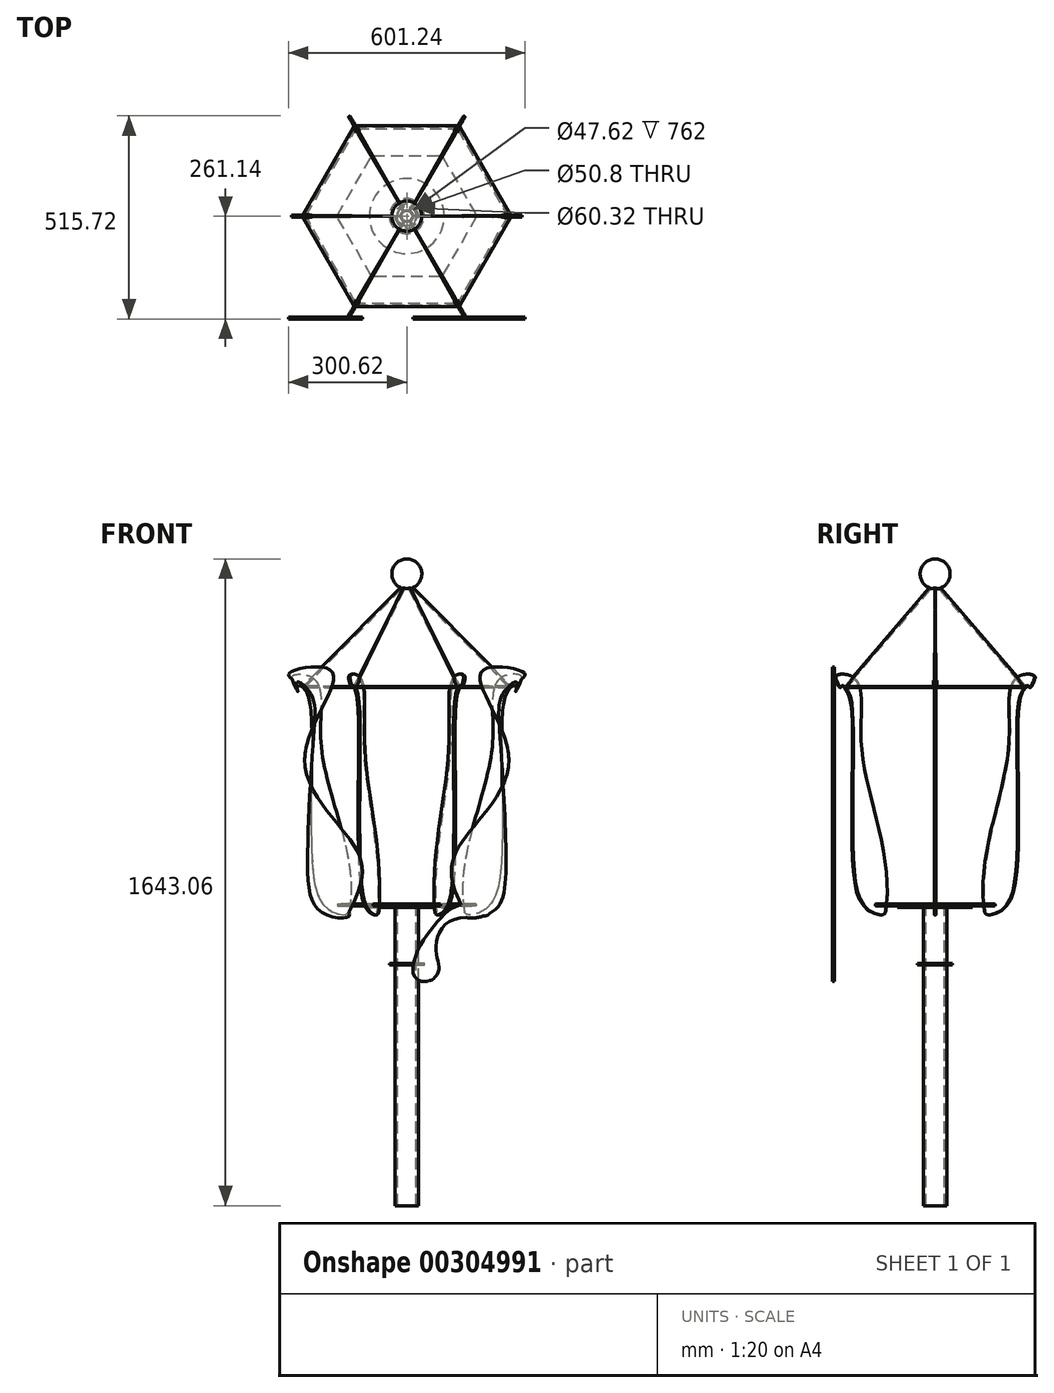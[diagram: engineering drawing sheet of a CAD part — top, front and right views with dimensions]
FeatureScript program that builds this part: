
annotation { "Feature Type Name" : "Feature", "Feature Type Description" : "" }
export const myFeature = defineFeature(function(context is Context, id is Id, definition is map)
    precondition{}
    {
        {
            var Q0;
            Q0=qCreatedBy(makeId("Front.planeOp"),FACE);
            var sketch = newSketch(context, id + "F0", { "sketchPlane" : qUnion([Q0])});
            skFitSpline(sketch, "E0", {"points": [v(-291.6, 220.03) * mm, v(-241.23, 224.84) * mm, v(-217, 46.23) * mm, v(-146.46, -370.89) * mm], "startDerivative": vector(-130.21, 261.55) * mm, "endDerivative": vector(-153.32, -857.59) * mm});
            skPoint(sketch, "E1.1.internal.snap0", {"position": v(-274.64, 203.2) * mm});
            skFitSpline(sketch, "E1", {"points": [v(-291.6, 220.03) * mm, v(-274.64, 203.2) * mm, v(-257.97, 191.77) * mm, v(-241.35, 95.06) * mm, v(-239.01, -260.8) * mm, v(-195.03, -367.33) * mm, v(-146.46, -370.89) * mm], "startDerivative": vector(512.54, -1083.48) * mm, "endDerivative": vector(69.83, 321.72) * mm});
            skPoint(sketch, "E2", {"position": v(-173.04, -355.6) * mm});
            skLineSegment(sketch, "E3", {"start": v(0, 533.4) * mm, "end": v(0, -533.4) * mm, "construction": true});
            skArc(sketch, "E4", {"start": v(0, 525.46) * mm, "mid": v(-38.1, 487.36) * mm, "end": v(0, 449.26) * mm});
            skLineSegment(sketch, "E5", {"start": v(0, 525.46) * mm, "end": v(0, 449.26) * mm});
            skPoint(sketch, "E6", {"position": v(0, 461.96) * mm});
            skLineSegment(sketch, "E7.bottom", {"start": v(-30.16, -355.6) * mm, "end": v(-23.81, -355.6) * mm});
            skLineSegment(sketch, "E7.top", {"start": v(-30.16, -1117.6) * mm, "end": v(-23.81, -1117.6) * mm});
            skLineSegment(sketch, "E7.left", {"start": v(-30.16, -355.6) * mm, "end": v(-30.16, -1117.6) * mm});
            skLineSegment(sketch, "E7.right", {"start": v(-23.81, -355.6) * mm, "end": v(-23.81, -1117.6) * mm});
            skFitSpline(sketch, "E8.MirrorCS", {"points": [v(291.6, 220.03) * mm, v(274.64, 203.2) * mm, v(257.97, 191.77) * mm, v(241.35, 95.06) * mm, v(239.01, -260.8) * mm, v(195.03, -367.33) * mm, v(146.46, -370.89) * mm], "startDerivative": vector(-512.54, -1083.48) * mm, "endDerivative": vector(-69.83, 321.72) * mm});
            skPoint(sketch, "E9.MirrorP", {"position": v(173.04, -355.6) * mm});
            skFitSpline(sketch, "E10.MirrorCS", {"points": [v(291.6, 220.03) * mm, v(241.23, 224.84) * mm, v(217, 46.23) * mm, v(146.46, -370.89) * mm], "startDerivative": vector(130.21, 261.55) * mm, "endDerivative": vector(153.32, -857.59) * mm});
            skLineSegment(sketch, "E11.MirrorCS", {"start": v(30.16, -355.6) * mm, "end": v(30.16, -1117.6) * mm});
            skLineSegment(sketch, "E12.MirrorCS", {"start": v(30.16, -355.6) * mm, "end": v(23.81, -355.6) * mm});
            skLineSegment(sketch, "E13.MirrorCS", {"start": v(23.81, -355.6) * mm, "end": v(23.81, -1117.6) * mm});
            skLineSegment(sketch, "E14.MirrorCS", {"start": v(30.16, -1117.6) * mm, "end": v(23.81, -1117.6) * mm});
            skFitSpline(sketch, "E15", {"points": [v(183.47, -350.73) * mm, v(204.81, -367.22) * mm, v(125.26, -406.15) * mm, v(80.03, -477) * mm, v(76.64, -518.47) * mm, v(56.5, -545.64) * mm, v(30.16, -533.12) * mm, v(33.54, -472.55) * mm, v(77.47, -401.03) * mm, v(128.65, -357.22) * mm, v(183.47, -350.73) * mm]});
            skSolve(sketch);
        }
        {
            var Q0;
            Q0=qCreatedBy(makeId("Top.planeOp"),FACE);
            cPlane(context, id + "F1", {"entities" : qUnion([Q0]), "cplaneType" : CPlaneType.OFFSET, "offset" : 355.6 * mm, "oppositeDirection" : true, "width" : 152.4 * mm, "height" : 152.4 * mm});
        }
        {
            var Q0;
            Q0=qCreatedBy(id+"F1.planeOp",FACE);
            var sketch = newSketch(context, id + "F2", { "sketchPlane" : qUnion([Q0])});
            skCircle(sketch, "E16.cCircle", {"center": v(0, 0) * mm, "radius": 177.8 * mm, "construction": true});
            skLineSegment(sketch, "E16.0", {"start": v(-177.8, 0) * mm, "end": v(-88.9, 153.98) * mm});
            skLineSegment(sketch, "E16.1", {"start": v(-88.9, 153.98) * mm, "end": v(88.9, 153.98) * mm});
            skLineSegment(sketch, "E16.2", {"start": v(88.9, 153.98) * mm, "end": v(177.8, 0) * mm});
            skLineSegment(sketch, "E16.3", {"start": v(177.8, 0) * mm, "end": v(88.9, -153.98) * mm});
            skLineSegment(sketch, "E16.4", {"start": v(88.9, -153.98) * mm, "end": v(-88.9, -153.98) * mm});
            skLineSegment(sketch, "E16.5", {"start": v(-88.9, -153.98) * mm, "end": v(-177.8, 0) * mm});
            skLineSegment(sketch, "E17", {"start": v(-176.43, 2.38) * mm, "end": v(-149.22, 2.38) * mm});
            skLineSegment(sketch, "E18", {"start": v(-149.22, 2.38) * mm, "end": v(-149.22, -2.38) * mm});
            skLineSegment(sketch, "E19", {"start": v(-149.22, -2.38) * mm, "end": v(-176.43, -2.38) * mm});
            skPoint(sketch, "E20.endSnap0", {"position": v(-149.22, 0) * mm});
            skLineSegment(sketch, "E21", {"start": v(0, 0) * mm, "end": v(-304.8, 0) * mm, "construction": true});
            skPoint(sketch, "E22.1.0", {"position": v(-74.61, -129.23) * mm});
            skLineSegment(sketch, "E22.1.1", {"start": v(-72.55, -130.42) * mm, "end": v(-86.15, -153.98) * mm});
            skLineSegment(sketch, "E22.1.2", {"start": v(-76.67, -128.04) * mm, "end": v(-72.55, -130.42) * mm});
            skLineSegment(sketch, "E22.1.3", {"start": v(-90.27, -151.6) * mm, "end": v(-76.67, -128.04) * mm});
            skPoint(sketch, "E22.2.0", {"position": v(74.61, -129.23) * mm});
            skLineSegment(sketch, "E22.2.1", {"start": v(76.67, -128.04) * mm, "end": v(90.27, -151.6) * mm});
            skLineSegment(sketch, "E22.2.2", {"start": v(72.55, -130.42) * mm, "end": v(76.67, -128.04) * mm});
            skLineSegment(sketch, "E22.2.3", {"start": v(86.15, -153.98) * mm, "end": v(72.55, -130.42) * mm});
            skPoint(sketch, "E23.0.3.0", {"position": v(149.22, 0) * mm});
            skLineSegment(sketch, "E23.1.3.0", {"start": v(149.22, 2.38) * mm, "end": v(176.43, 2.38) * mm});
            skLineSegment(sketch, "E23.4.3.0", {"start": v(149.22, -2.38) * mm, "end": v(149.22, 2.38) * mm});
            skLineSegment(sketch, "E23.7.3.0", {"start": v(176.43, -2.38) * mm, "end": v(149.22, -2.38) * mm});
            skPoint(sketch, "E23.0.4.0", {"position": v(74.61, 129.23) * mm});
            skLineSegment(sketch, "E23.1.4.0", {"start": v(72.55, 130.42) * mm, "end": v(86.15, 153.98) * mm});
            skLineSegment(sketch, "E23.4.4.0", {"start": v(76.67, 128.04) * mm, "end": v(72.55, 130.42) * mm});
            skLineSegment(sketch, "E23.7.4.0", {"start": v(90.27, 151.6) * mm, "end": v(76.67, 128.04) * mm});
            skPoint(sketch, "E23.0.5.0", {"position": v(-74.61, 129.23) * mm});
            skLineSegment(sketch, "E23.1.5.0", {"start": v(-76.67, 128.04) * mm, "end": v(-90.27, 151.6) * mm});
            skLineSegment(sketch, "E23.4.5.0", {"start": v(-72.55, 130.42) * mm, "end": v(-76.67, 128.04) * mm});
            skLineSegment(sketch, "E23.7.5.0", {"start": v(-86.15, 153.98) * mm, "end": v(-72.55, 130.42) * mm});
            skSolve(sketch);
        }
        {
            var Q0;
            {var subQ11=sQuery(id+"F2.wireOp",EDGE,"E17");Q0=makeQuery(id+"F2.imprint","IMPRINT",FACE,{"disambiguationData":[TD([[makeQuery(id+"F2.imprint","IMPRINT",EDGE,{"derivedFrom":subQ11}),1.0]])]});}
            extrude(context, id + "F3", {"entities" : qUnion([Q0]), "depth" : 4.76 * mm});
        }
        {
            var Q0;
            Q0=qCreatedBy(makeId("Top.planeOp"),FACE);
            cPlane(context, id + "F4", {"entities" : qUnion([Q0]), "cplaneType" : CPlaneType.OFFSET, "offset" : 203.2 * mm, "width" : 152.4 * mm, "height" : 152.4 * mm});
        }
        {
            var Q0;
            Q0=qCreatedBy(id+"F4.planeOp",FACE);
            var sketch = newSketch(context, id + "F5", { "sketchPlane" : qUnion([Q0])});
            skCircle(sketch, "E24.cCircle", {"center": v(0, 0) * mm, "radius": 222.25 * mm, "construction": true});
            skLineSegment(sketch, "E24.0", {"start": v(-128.32, -222.25) * mm, "end": v(-256.63, 0) * mm});
            skLineSegment(sketch, "E24.1", {"start": v(-256.63, 0) * mm, "end": v(-128.32, 222.25) * mm});
            skLineSegment(sketch, "E24.2", {"start": v(-128.32, 222.25) * mm, "end": v(128.32, 222.25) * mm});
            skLineSegment(sketch, "E24.3", {"start": v(128.32, 222.25) * mm, "end": v(256.63, 0) * mm});
            skLineSegment(sketch, "E24.4", {"start": v(256.63, 0) * mm, "end": v(128.32, -222.25) * mm});
            skLineSegment(sketch, "E24.5", {"start": v(128.32, -222.25) * mm, "end": v(-128.32, -222.25) * mm});
            skPoint(sketch, "E24.0.midPoint", {"position": v(-192.47, -111.12) * mm});
            skLineSegment(sketch, "E25", {"start": v(-255.26, -2.38) * mm, "end": v(-231.23, -2.38) * mm});
            skLineSegment(sketch, "E26", {"start": v(-231.23, -2.38) * mm, "end": v(-231.23, 2.38) * mm});
            skLineSegment(sketch, "E27", {"start": v(-231.23, 2.38) * mm, "end": v(-255.26, 2.38) * mm});
            skLineSegment(sketch, "E28", {"start": v(0, 0) * mm, "end": v(-304.8, 0) * mm, "construction": true});
            skPoint(sketch, "E29", {"position": v(-231.23, 0) * mm});
            skPoint(sketch, "E30.1.0", {"position": v(-115.62, -200.25) * mm});
            skLineSegment(sketch, "E30.1.1", {"start": v(-125.57, -222.25) * mm, "end": v(-113.55, -201.44) * mm});
            skLineSegment(sketch, "E30.1.2", {"start": v(-117.68, -199.06) * mm, "end": v(-129.7, -219.87) * mm});
            skLineSegment(sketch, "E30.1.3", {"start": v(-113.55, -201.44) * mm, "end": v(-117.68, -199.06) * mm});
            skPoint(sketch, "E30.2.0", {"position": v(115.62, -200.25) * mm});
            skLineSegment(sketch, "E30.2.1", {"start": v(129.7, -219.87) * mm, "end": v(117.68, -199.06) * mm});
            skLineSegment(sketch, "E30.2.2", {"start": v(113.55, -201.44) * mm, "end": v(125.57, -222.25) * mm});
            skLineSegment(sketch, "E30.2.3", {"start": v(117.68, -199.06) * mm, "end": v(113.55, -201.44) * mm});
            skPoint(sketch, "E30.3.0", {"position": v(231.23, 0) * mm});
            skLineSegment(sketch, "E30.3.1", {"start": v(255.26, 2.38) * mm, "end": v(231.23, 2.38) * mm});
            skLineSegment(sketch, "E30.3.2", {"start": v(231.23, -2.38) * mm, "end": v(255.26, -2.38) * mm});
            skLineSegment(sketch, "E30.3.3", {"start": v(231.23, 2.38) * mm, "end": v(231.23, -2.38) * mm});
            skPoint(sketch, "E30.4.0", {"position": v(115.62, 200.25) * mm});
            skLineSegment(sketch, "E30.4.1", {"start": v(125.57, 222.25) * mm, "end": v(113.55, 201.44) * mm});
            skLineSegment(sketch, "E30.4.2", {"start": v(117.68, 199.06) * mm, "end": v(129.7, 219.87) * mm});
            skLineSegment(sketch, "E30.4.3", {"start": v(113.55, 201.44) * mm, "end": v(117.68, 199.06) * mm});
            skPoint(sketch, "E30.5.0", {"position": v(-115.62, 200.25) * mm});
            skLineSegment(sketch, "E30.5.1", {"start": v(-129.7, 219.87) * mm, "end": v(-117.68, 199.06) * mm});
            skLineSegment(sketch, "E30.5.2", {"start": v(-113.55, 201.44) * mm, "end": v(-125.57, 222.25) * mm});
            skLineSegment(sketch, "E30.5.3", {"start": v(-117.68, 199.06) * mm, "end": v(-113.55, 201.44) * mm});
            skSolve(sketch);
        }
        {
            var Q0;
            {var subQ11=sQuery(id+"F5.wireOp",EDGE,"E25");Q0=makeQuery(id+"F5.imprint","IMPRINT",FACE,{"disambiguationData":[TD([[makeQuery(id+"F5.imprint","IMPRINT",EDGE,{"derivedFrom":subQ11}),-1.0]])]});}
            extrude(context, id + "F6", {"entities" : qUnion([Q0]), "oppositeDirection" : true, "depth" : 4.76 * mm});
        }
        {
            var Q0;
            Q0=makeQuery(id+"F0.imprint","IMPRINT",FACE,{"disambiguationData":[TD([[makeQuery(id+"F0.imprint","IMPRINT",EDGE,{"derivedFrom":sQuery(id+"F0.wireOp",EDGE,"E0")}),-1.0]])]});
            var Q1;
            {var subQ1=sQuery(id+"F0.wireOp",EDGE,"E8.MirrorCS");Q1=makeQuery(id+"F0.imprint","IMPRINT",FACE,{"disambiguationData":[TD([[makeQuery(id+"F0.imprint","IMPRINT",EDGE,{"derivedFrom":subQ1}),-1.0]])]});}
            extrude(context, id + "F7", {"entities" : qUnion([Q0, Q1]), "endBound" : BoundingType.SYMMETRIC, "depth" : 4.76 * mm});
        }
        {
            var Q0;
            Q0=makeQuery(id+"F7.opExtrude","SWEPT_BODY",BODY,{"disambiguationData":[OSD([sQuery(id+"F0.wireOp",EDGE,"E0"),sQuery(id+"F0.wireOp",EDGE,"E1")])]});
            var Q1;
            Q1=makeQuery(id+"F7.opExtrude","SWEPT_BODY",BODY,{"disambiguationData":[OSD([sQuery(id+"F0.wireOp",EDGE,"E8.MirrorCS"),sQuery(id+"F0.wireOp",EDGE,"E10.MirrorCS"),sQuery(id+"F0.wireOp",EDGE,"E11.MirrorCS"),sQuery(id+"F0.wireOp",EDGE,"E15")])]});
            var Q2;
            Q2=sQuery(id+"F0.wireOp",EDGE,"E3");
            circularPattern(context, id + "F8", {"entities" : qUnion([Q0, Q1]), "axis" : qUnion([Q2]), "angle" : 360 * degree, "instanceCount" : 3, "equalSpace" : true});
        }
        {
            var Q0;
            Q0=makeQuery(id+"F0.imprint","IMPRINT",FACE,{"disambiguationData":[TD([[makeQuery(id+"F0.imprint","IMPRINT",EDGE,{"derivedFrom":sQuery(id+"F0.wireOp",EDGE,"E4")}),1.0]])]});
            var Q1;
            Q1=makeQuery(id+"F0.imprint","IMPRINT",FACE,{"disambiguationData":[TD([[makeQuery(id+"F0.imprint","IMPRINT",EDGE,{"derivedFrom":sQuery(id+"F0.wireOp",EDGE,"E7.bottom")}),-1.0]])]});
            var Q2;
            Q2=sQuery(id+"F0.wireOp",EDGE,"E3");
            revolve(context, id + "F9", {"entities" : qUnion([Q0, Q1]), "axis" : qUnion([Q2]), "revolveType" : RevolveType.FULL});
        }
        {
            var Q0;
            Q0=makeQuery(id+"F6.opExtrude","CAP_VERTEX",VERTEX,{"disambiguationData":[OSD([sQuery(id+"F5.wireOp",EDGE,"E24.0"),sQuery(id+"F5.wireOp",EDGE,"E25")])],"isStart":true});
            var Q1;
            Q1=makeQuery(id+"F6.opExtrude","CAP_VERTEX",VERTEX,{"disambiguationData":[OSD([sQuery(id+"F5.wireOp",EDGE,"E24.0"),sQuery(id+"F5.wireOp",EDGE,"E30.1.2")])],"isStart":true});
            var Q2;
            Q2=sQuery(id+"F0.wireOp",VERTEX,"E6");
            cPlane(context, id + "F10", {"entities" : qUnion([Q0, Q1, Q2]), "cplaneType" : CPlaneType.THREE_POINT, "offset" : 25.4 * mm, "width" : 152.4 * mm, "height" : 152.4 * mm});
        }
        {
            var Q0;
            Q0=qCreatedBy(id+"F10.planeOp",FACE);
            var sketch = newSketch(context, id + "F11", { "sketchPlane" : qUnion([Q0])});
            skLineSegment(sketch, "E31.0.7", {"start": v(120.81, -35.47) * mm, "end": v(-114.24, 52.95) * mm, "construction": true});
            skPoint(sketch, "E32.0", {"position": v(123.39, 328) * mm});
            skLineSegment(sketch, "E33", {"start": v(123.39, 328) * mm, "end": v(-114.24, 52.95) * mm, "construction": true});
            skLineSegment(sketch, "E34", {"start": v(120.81, -35.47) * mm, "end": v(123.39, 328) * mm, "construction": true});
            skLineSegment(sketch, "E35.0", {"start": v(108.66, 314.6) * mm, "end": v(-105.95, 66.2) * mm});
            skLineSegment(sketch, "E35.1", {"start": v(123.3, -20.05) * mm, "end": v(125.63, 308.21) * mm});
            skLineSegment(sketch, "E35.2", {"start": v(120.81, -42.25) * mm, "end": v(-118.7, 47.85) * mm});
            skPoint(sketch, "E36.0", {"position": v(130.17, 346.04) * mm});
            skArc(sketch, "E37", {"start": v(125.63, 308.21) * mm, "mid": v(116.76, 310.38) * mm, "end": v(108.66, 314.6) * mm});
            skLineSegment(sketch, "E38", {"start": v(123.3, -20.05) * mm, "end": v(120.92, -20.03) * mm});
            skLineSegment(sketch, "E39", {"start": v(120.92, -20.03) * mm, "end": v(120.81, -42.25) * mm});
            skLineSegment(sketch, "E40", {"start": v(130.17, 346.04) * mm, "end": v(3.29, 8.74) * mm, "construction": true});
            skPoint(sketch, "E40.endSnap0", {"position": v(3.29, 8.74) * mm});
            skLineSegment(sketch, "E41.MirrorCS", {"start": v(-105.95, 66.2) * mm, "end": v(-104.14, 64.64) * mm});
            skLineSegment(sketch, "E42.MirrorCS", {"start": v(-104.14, 64.64) * mm, "end": v(-118.7, 47.85) * mm});
            skSolve(sketch);
        }
        {
            var Q0;
            {var subQ0=sQuery(id+"F11.wireOp",EDGE,"E35.0");var subQ1=sQuery(id+"F11.wireOp",EDGE,"E31.0.19");var subQ2=makeQuery(id+"F11.imprint","INTERSECT",VERTEX,{"derivedFrom":[subQ1,subQ0]});Q0=makeQuery(id+"F11.imprint","IMPRINT",FACE,{"disambiguationData":[TD([[makeQuery(id+"F11.imprint","IMPRINT",EDGE,{"disambiguationData":[TD([[subQ2,-1.0]])],"derivedFrom":subQ1}),1.0]])]});}
            var Q1;
            {var subQ0=sQuery(id+"F11.wireOp",EDGE,"E35.2");Q1=makeQuery(id+"F11.imprint","IMPRINT",FACE,{"disambiguationData":[TD([[makeQuery(id+"F11.imprint","IMPRINT",EDGE,{"derivedFrom":subQ0}),-1.0]])]});}
            extrude(context, id + "F12", {"entities" : qUnion([Q0, Q1]), "oppositeDirection" : true, "depth" : 4.76 * mm});
        }
        {
            var Q0;
            Q0=makeQuery(id+"F12.opExtrude","SWEPT_BODY",BODY,{"disambiguationData":[OSD([sQuery(id+"F11.wireOp",EDGE,"E35.0"),sQuery(id+"F11.wireOp",EDGE,"E35.1"),sQuery(id+"F11.wireOp",EDGE,"E35.2"),sQuery(id+"F11.wireOp",EDGE,"E37")])]});
            var Q1;
            Q1=sQuery(id+"F0.wireOp",EDGE,"E3");
            circularPattern(context, id + "F13", {"entities" : qUnion([Q0]), "axis" : qUnion([Q1]), "angle" : 360 * degree, "instanceCount" : 6, "equalSpace" : true});
        }
        {
            var Q0;
            Q0=makeQuery(id+"F3.opExtrude","CAP_FACE",FACE,{"disambiguationData":[OSD([sQuery(id+"F2.wireOp",EDGE,"E16.0"),sQuery(id+"F2.wireOp",EDGE,"E16.1"),sQuery(id+"F2.wireOp",EDGE,"E16.2"),sQuery(id+"F2.wireOp",EDGE,"E16.3"),sQuery(id+"F2.wireOp",EDGE,"E16.4"),sQuery(id+"F2.wireOp",EDGE,"E16.5"),sQuery(id+"F2.wireOp",EDGE,"E17"),sQuery(id+"F2.wireOp",EDGE,"E18"),sQuery(id+"F2.wireOp",EDGE,"E19"),sQuery(id+"F2.wireOp",EDGE,"E22.1.1"),sQuery(id+"F2.wireOp",EDGE,"E22.1.2"),sQuery(id+"F2.wireOp",EDGE,"E22.1.3"),sQuery(id+"F2.wireOp",EDGE,"E22.2.1"),sQuery(id+"F2.wireOp",EDGE,"E22.2.2"),sQuery(id+"F2.wireOp",EDGE,"E22.2.3"),sQuery(id+"F2.wireOp",EDGE,"E23.1.3.0"),sQuery(id+"F2.wireOp",EDGE,"E23.4.3.0"),sQuery(id+"F2.wireOp",EDGE,"E23.7.3.0"),sQuery(id+"F2.wireOp",EDGE,"E23.1.4.0"),sQuery(id+"F2.wireOp",EDGE,"E23.4.4.0"),sQuery(id+"F2.wireOp",EDGE,"E23.7.4.0"),sQuery(id+"F2.wireOp",EDGE,"E23.1.5.0"),sQuery(id+"F2.wireOp",EDGE,"E23.4.5.0"),sQuery(id+"F2.wireOp",EDGE,"E23.7.5.0")])],"isStart":true});
            var sketch = newSketch(context, id + "F14", { "sketchPlane" : qUnion([Q0])});
            skCircle(sketch, "E43.0", {"center": v(0, 0) * mm, "radius": 23.81 * mm});
            skCircle(sketch, "E44", {"center": v(0, 0) * mm, "radius": 23.1 * mm});
            skCircle(sketch, "E45", {"center": v(0, 0) * mm, "radius": 30.16 * mm});
            skCircle(sketch, "E46", {"center": v(0, 0) * mm, "radius": 95.25 * mm});
            skSolve(sketch);
        }
        {
            var Q0;
            Q0=sQuery(id+"F14.wireOp",VERTEX,"E46.center");
            var Q1;
            Q1=makeQuery(id+"F3.opExtrude","SWEPT_BODY",BODY,{"disambiguationData":[OSD([sQuery(id+"F2.wireOp",EDGE,"E16.0"),sQuery(id+"F2.wireOp",EDGE,"E16.1"),sQuery(id+"F2.wireOp",EDGE,"E16.2"),sQuery(id+"F2.wireOp",EDGE,"E16.3"),sQuery(id+"F2.wireOp",EDGE,"E16.4"),sQuery(id+"F2.wireOp",EDGE,"E16.5"),sQuery(id+"F2.wireOp",EDGE,"E17"),sQuery(id+"F2.wireOp",EDGE,"E18"),sQuery(id+"F2.wireOp",EDGE,"E19"),sQuery(id+"F2.wireOp",EDGE,"E22.1.1"),sQuery(id+"F2.wireOp",EDGE,"E22.1.2"),sQuery(id+"F2.wireOp",EDGE,"E22.1.3"),sQuery(id+"F2.wireOp",EDGE,"E22.2.1"),sQuery(id+"F2.wireOp",EDGE,"E22.2.2"),sQuery(id+"F2.wireOp",EDGE,"E22.2.3"),sQuery(id+"F2.wireOp",EDGE,"E23.1.3.0"),sQuery(id+"F2.wireOp",EDGE,"E23.4.3.0"),sQuery(id+"F2.wireOp",EDGE,"E23.7.3.0"),sQuery(id+"F2.wireOp",EDGE,"E23.1.4.0"),sQuery(id+"F2.wireOp",EDGE,"E23.4.4.0"),sQuery(id+"F2.wireOp",EDGE,"E23.7.4.0"),sQuery(id+"F2.wireOp",EDGE,"E23.1.5.0"),sQuery(id+"F2.wireOp",EDGE,"E23.4.5.0"),sQuery(id+"F2.wireOp",EDGE,"E23.7.5.0")])]});
            hole(context, id + "F15", {"style" : HoleStyle.SIMPLE, "endStyle" : HoleEndStyle.THROUGH, "holeDiameter" : 50.8 * mm, "tappedDepth" : 12.7 * mm, "tapClearance" : 3, "locations" : qUnion([Q0]), "scope" : qUnion([Q1])});
        }
        {
            var Q0;
            Q0 = qSketchRegion(id + "F14", true);
            extrude(context, id + "F16", {"entities" : qUnion([Q0]), "depth" : 4.76 * mm});
        }
        {
            var Q0;
            Q0=qCreatedBy(makeId("Top.planeOp"),FACE);
            cPlane(context, id + "F17", {"entities" : qUnion([Q0]), "cplaneType" : CPlaneType.OFFSET, "offset" : 501.65 * mm, "oppositeDirection" : true, "width" : 152.4 * mm, "height" : 152.4 * mm});
        }
        {
            var Q0;
            Q0=qCreatedBy(id+"F17.planeOp",FACE);
            var sketch = newSketch(context, id + "F18", { "sketchPlane" : qUnion([Q0])});
            skCircle(sketch, "E47", {"center": v(0, 0) * mm, "radius": 44.45 * mm});
            skLineSegment(sketch, "E48", {"start": v(44.39, -2.38) * mm, "end": v(38.04, -2.38) * mm});
            skLineSegment(sketch, "E49", {"start": v(38.04, -2.38) * mm, "end": v(38.04, 2.38) * mm});
            skLineSegment(sketch, "E50", {"start": v(38.04, 2.38) * mm, "end": v(44.39, 2.38) * mm});
            skLineSegment(sketch, "E51", {"start": v(0, 0) * mm, "end": v(-76.2, 0) * mm, "construction": true});
            skPoint(sketch, "E52", {"position": v(38.04, 0) * mm});
            skPoint(sketch, "E53.1.0", {"position": v(-19.02, 32.94) * mm});
            skLineSegment(sketch, "E53.1.1", {"start": v(-20.13, 39.63) * mm, "end": v(-16.96, 34.13) * mm});
            skLineSegment(sketch, "E53.1.2", {"start": v(-21.08, 31.75) * mm, "end": v(-24.26, 37.25) * mm});
            skLineSegment(sketch, "E53.1.3", {"start": v(-16.96, 34.13) * mm, "end": v(-21.08, 31.75) * mm});
            skPoint(sketch, "E53.2.0", {"position": v(-19.02, -32.94) * mm});
            skLineSegment(sketch, "E53.2.1", {"start": v(-24.26, -37.25) * mm, "end": v(-21.08, -31.75) * mm});
            skLineSegment(sketch, "E53.2.2", {"start": v(-16.96, -34.13) * mm, "end": v(-20.13, -39.63) * mm});
            skLineSegment(sketch, "E53.2.3", {"start": v(-21.08, -31.75) * mm, "end": v(-16.96, -34.13) * mm});
            skSolve(sketch);
        }
        {
            var Q0;
            {var subQ5=sQuery(id+"F18.wireOp",EDGE,"E48");Q0=makeQuery(id+"F18.imprint","IMPRINT",FACE,{"disambiguationData":[TD([[makeQuery(id+"F18.imprint","IMPRINT",EDGE,{"derivedFrom":subQ5}),1.0]])]});}
            extrude(context, id + "F19", {"entities" : qUnion([Q0]), "oppositeDirection" : true, "depth" : 4.76 * mm});
        }
        {
            var Q0;
            Q0=makeQuery(id+"F13.opPattern","COPY",BODY,{"derivedFrom":makeQuery(id+"F12.opExtrude","SWEPT_BODY",BODY,{"disambiguationData":[OSD([sQuery(id+"F11.wireOp",EDGE,"E35.0"),sQuery(id+"F11.wireOp",EDGE,"E35.1"),sQuery(id+"F11.wireOp",EDGE,"E35.2"),sQuery(id+"F11.wireOp",EDGE,"E37")])]}),"instanceName":"2"});
            var Q1;
            Q1=makeQuery(id+"F13.opPattern","COPY",BODY,{"derivedFrom":makeQuery(id+"F12.opExtrude","SWEPT_BODY",BODY,{"disambiguationData":[OSD([sQuery(id+"F11.wireOp",EDGE,"E35.0"),sQuery(id+"F11.wireOp",EDGE,"E35.1"),sQuery(id+"F11.wireOp",EDGE,"E35.2"),sQuery(id+"F11.wireOp",EDGE,"E37")])]}),"instanceName":"3"});
            var Q2;
            Q2=makeQuery(id+"F13.opPattern","COPY",BODY,{"derivedFrom":makeQuery(id+"F12.opExtrude","SWEPT_BODY",BODY,{"disambiguationData":[OSD([sQuery(id+"F11.wireOp",EDGE,"E35.0"),sQuery(id+"F11.wireOp",EDGE,"E35.1"),sQuery(id+"F11.wireOp",EDGE,"E35.2"),sQuery(id+"F11.wireOp",EDGE,"E37")])]}),"instanceName":"4"});
            var Q3;
            Q3=makeQuery(id+"F13.opPattern","COPY",BODY,{"derivedFrom":makeQuery(id+"F12.opExtrude","SWEPT_BODY",BODY,{"disambiguationData":[OSD([sQuery(id+"F11.wireOp",EDGE,"E35.0"),sQuery(id+"F11.wireOp",EDGE,"E35.1"),sQuery(id+"F11.wireOp",EDGE,"E35.2"),sQuery(id+"F11.wireOp",EDGE,"E37")])]}),"instanceName":"5"});
            var Q4;
            Q4=makeQuery(id+"F12.opExtrude","SWEPT_BODY",BODY,{"disambiguationData":[OSD([sQuery(id+"F11.wireOp",EDGE,"E35.0"),sQuery(id+"F11.wireOp",EDGE,"E35.1"),sQuery(id+"F11.wireOp",EDGE,"E35.2"),sQuery(id+"F11.wireOp",EDGE,"E37")])]});
            var Q5;
            Q5=makeQuery(id+"F13.opPattern","COPY",BODY,{"derivedFrom":makeQuery(id+"F12.opExtrude","SWEPT_BODY",BODY,{"disambiguationData":[OSD([sQuery(id+"F11.wireOp",EDGE,"E35.0"),sQuery(id+"F11.wireOp",EDGE,"E35.1"),sQuery(id+"F11.wireOp",EDGE,"E35.2"),sQuery(id+"F11.wireOp",EDGE,"E37")])]}),"instanceName":"1"});
            var Q6;
            Q6=makeQuery(id+"F3.opExtrude","SWEPT_BODY",BODY,{"disambiguationData":[OSD([sQuery(id+"F2.wireOp",EDGE,"E16.0"),sQuery(id+"F2.wireOp",EDGE,"E16.1"),sQuery(id+"F2.wireOp",EDGE,"E16.2"),sQuery(id+"F2.wireOp",EDGE,"E16.3"),sQuery(id+"F2.wireOp",EDGE,"E16.4"),sQuery(id+"F2.wireOp",EDGE,"E16.5"),sQuery(id+"F2.wireOp",EDGE,"E17"),sQuery(id+"F2.wireOp",EDGE,"E18"),sQuery(id+"F2.wireOp",EDGE,"E19"),sQuery(id+"F2.wireOp",EDGE,"E22.1.1"),sQuery(id+"F2.wireOp",EDGE,"E22.1.2"),sQuery(id+"F2.wireOp",EDGE,"E22.1.3"),sQuery(id+"F2.wireOp",EDGE,"E22.2.1"),sQuery(id+"F2.wireOp",EDGE,"E22.2.2"),sQuery(id+"F2.wireOp",EDGE,"E22.2.3"),sQuery(id+"F2.wireOp",EDGE,"E23.1.3.0"),sQuery(id+"F2.wireOp",EDGE,"E23.4.3.0"),sQuery(id+"F2.wireOp",EDGE,"E23.7.3.0"),sQuery(id+"F2.wireOp",EDGE,"E23.1.4.0"),sQuery(id+"F2.wireOp",EDGE,"E23.4.4.0"),sQuery(id+"F2.wireOp",EDGE,"E23.7.4.0"),sQuery(id+"F2.wireOp",EDGE,"E23.1.5.0"),sQuery(id+"F2.wireOp",EDGE,"E23.4.5.0"),sQuery(id+"F2.wireOp",EDGE,"E23.7.5.0")])]});
            var Q7;
            Q7=makeQuery(id+"F6.opExtrude","SWEPT_BODY",BODY,{"disambiguationData":[OSD([sQuery(id+"F5.wireOp",EDGE,"E24.0"),sQuery(id+"F5.wireOp",EDGE,"E24.1"),sQuery(id+"F5.wireOp",EDGE,"E24.2"),sQuery(id+"F5.wireOp",EDGE,"E24.3"),sQuery(id+"F5.wireOp",EDGE,"E24.4"),sQuery(id+"F5.wireOp",EDGE,"E24.5"),sQuery(id+"F5.wireOp",EDGE,"E25"),sQuery(id+"F5.wireOp",EDGE,"E26"),sQuery(id+"F5.wireOp",EDGE,"E27"),sQuery(id+"F5.wireOp",EDGE,"E30.1.1"),sQuery(id+"F5.wireOp",EDGE,"E30.1.2"),sQuery(id+"F5.wireOp",EDGE,"E30.1.3"),sQuery(id+"F5.wireOp",EDGE,"E30.2.1"),sQuery(id+"F5.wireOp",EDGE,"E30.2.2"),sQuery(id+"F5.wireOp",EDGE,"E30.2.3"),sQuery(id+"F5.wireOp",EDGE,"E30.3.1"),sQuery(id+"F5.wireOp",EDGE,"E30.3.2"),sQuery(id+"F5.wireOp",EDGE,"E30.3.3"),sQuery(id+"F5.wireOp",EDGE,"E30.4.1"),sQuery(id+"F5.wireOp",EDGE,"E30.4.2"),sQuery(id+"F5.wireOp",EDGE,"E30.4.3"),sQuery(id+"F5.wireOp",EDGE,"E30.5.1"),sQuery(id+"F5.wireOp",EDGE,"E30.5.2"),sQuery(id+"F5.wireOp",EDGE,"E30.5.3")])]});
            var Q8;
            Q8=makeQuery(id+"F19.opExtrude","SWEPT_BODY",BODY,{"disambiguationData":[OSD([sQuery(id+"F18.wireOp",EDGE,"E47"),sQuery(id+"F18.wireOp",EDGE,"E48"),sQuery(id+"F18.wireOp",EDGE,"E49"),sQuery(id+"F18.wireOp",EDGE,"E50"),sQuery(id+"F18.wireOp",EDGE,"E53.1.1"),sQuery(id+"F18.wireOp",EDGE,"E53.1.2"),sQuery(id+"F18.wireOp",EDGE,"E53.1.3"),sQuery(id+"F18.wireOp",EDGE,"E53.2.1"),sQuery(id+"F18.wireOp",EDGE,"E53.2.2"),sQuery(id+"F18.wireOp",EDGE,"E53.2.3")])]});
            var Q9;
            Q9=makeQuery(id+"F9.opRevolve","SWEPT_BODY",BODY,{"disambiguationData":[OSD([sQuery(id+"F0.wireOp",EDGE,"E7.bottom"),sQuery(id+"F0.wireOp",EDGE,"E7.top"),sQuery(id+"F0.wireOp",EDGE,"E7.left"),sQuery(id+"F0.wireOp",EDGE,"E7.right")])]});
            var Q10;
            Q10=makeQuery(id+"F7.opExtrude","SWEPT_BODY",BODY,{"disambiguationData":[OSD([sQuery(id+"F0.wireOp",EDGE,"E0"),sQuery(id+"F0.wireOp",EDGE,"E1")])]});
            var Q11;
            Q11=makeQuery(id+"F8.opPattern","COPY",BODY,{"derivedFrom":makeQuery(id+"F7.opExtrude","SWEPT_BODY",BODY,{"disambiguationData":[OSD([sQuery(id+"F0.wireOp",EDGE,"E8.MirrorCS"),sQuery(id+"F0.wireOp",EDGE,"E10.MirrorCS"),sQuery(id+"F0.wireOp",EDGE,"E11.MirrorCS"),sQuery(id+"F0.wireOp",EDGE,"E15")])]}),"instanceName":"1"});
            var Q12;
            Q12=makeQuery(id+"F8.opPattern","COPY",BODY,{"derivedFrom":makeQuery(id+"F7.opExtrude","SWEPT_BODY",BODY,{"disambiguationData":[OSD([sQuery(id+"F0.wireOp",EDGE,"E0"),sQuery(id+"F0.wireOp",EDGE,"E1")])]}),"instanceName":"2"});
            var Q13;
            Q13=makeQuery(id+"F7.opExtrude","SWEPT_BODY",BODY,{"disambiguationData":[OSD([sQuery(id+"F0.wireOp",EDGE,"E8.MirrorCS"),sQuery(id+"F0.wireOp",EDGE,"E10.MirrorCS"),sQuery(id+"F0.wireOp",EDGE,"E11.MirrorCS"),sQuery(id+"F0.wireOp",EDGE,"E15")])]});
            var Q14;
            Q14=makeQuery(id+"F8.opPattern","COPY",BODY,{"derivedFrom":makeQuery(id+"F7.opExtrude","SWEPT_BODY",BODY,{"disambiguationData":[OSD([sQuery(id+"F0.wireOp",EDGE,"E0"),sQuery(id+"F0.wireOp",EDGE,"E1")])]}),"instanceName":"1"});
            var Q15;
            Q15=makeQuery(id+"F8.opPattern","COPY",BODY,{"derivedFrom":makeQuery(id+"F7.opExtrude","SWEPT_BODY",BODY,{"disambiguationData":[OSD([sQuery(id+"F0.wireOp",EDGE,"E8.MirrorCS"),sQuery(id+"F0.wireOp",EDGE,"E10.MirrorCS"),sQuery(id+"F0.wireOp",EDGE,"E11.MirrorCS"),sQuery(id+"F0.wireOp",EDGE,"E15")])]}),"instanceName":"2"});
            booleanBodies(context, id + "F20", {"operationType" : BooleanOperationType.SUBTRACTION, "tools" : qUnion([Q0, Q1, Q2, Q3, Q4, Q5, Q6, Q7, Q8, Q9]), "targets" : qUnion([Q10, Q11, Q12, Q13, Q14, Q15]), "keepTools" : true});
        }
        {
            var Q0;
            Q0=makeQuery(id+"F7.opExtrude","CAP_FACE",FACE,{"disambiguationData":[OSD([sQuery(id+"F0.wireOp",EDGE,"E0"),sQuery(id+"F0.wireOp",EDGE,"E1")])],"isStart":false});
            var sketch = newSketch(context, id + "F21", { "sketchPlane" : qUnion([Q0])});
            skLineSegment(sketch, "E54.1.1", {"start": v(255.26, 203.2) * mm, "end": v(244.38, 214.16) * mm, "construction": true});
            skLineSegment(sketch, "E54.1.3", {"start": v(204.78, 203.2) * mm, "end": v(223.83, 203.2) * mm});
            skLineSegment(sketch, "E54.1.4", {"start": v(231.23, 203.2) * mm, "end": v(231.23, 198.44) * mm});
            skLineSegment(sketch, "E54.1.5", {"start": v(231.23, 198.44) * mm, "end": v(222.22, 198.44) * mm});
            skFitSpline(sketch, "E54.1.6", {"points": [v(291.6, 220.03) * mm, v(299.11, 235.11) * mm, v(190.89, 240.63) * mm, v(259.32, 16.49) * mm, v(120.9, -227.85) * mm, v(146.46, -370.89) * mm]});
            skLineSegment(sketch, "E54.1.7", {"start": v(143.58, -350.84) * mm, "end": v(149.22, -350.84) * mm});
            skLineSegment(sketch, "E54.1.8", {"start": v(149.22, -350.84) * mm, "end": v(149.22, -355.6) * mm});
            skLineSegment(sketch, "E54.1.9", {"start": v(149.22, -355.6) * mm, "end": v(132.22, -355.6) * mm});
            skFitSpline(sketch, "E54.1.10", {"points": [v(143.66, -351.57) * mm, v(138.54, -353) * mm, v(113.49, -362.44) * mm, v(74.94, -400.1) * mm, v(29.16, -466.89) * mm, v(19.52, -535.33) * mm, v(47.3, -548.4) * mm, v(56.5, -545.64) * mm]});
            skLineSegment(sketch, "E54.1.11", {"start": v(30.16, -482.64) * mm, "end": v(30.16, -501.65) * mm});
            skLineSegment(sketch, "E54.1.12", {"start": v(30.16, -501.65) * mm, "end": v(38.04, -501.65) * mm});
            skLineSegment(sketch, "E54.1.13", {"start": v(38.04, -501.65) * mm, "end": v(38.04, -506.41) * mm});
            skLineSegment(sketch, "E54.1.14", {"start": v(38.04, -506.41) * mm, "end": v(30.16, -506.41) * mm});
            skLineSegment(sketch, "E54.1.15", {"start": v(30.16, -506.41) * mm, "end": v(30.16, -533.12) * mm});
            skFitSpline(sketch, "E54.1.16", {"points": [v(143.66, -351.57) * mm, v(138.54, -353) * mm, v(113.49, -362.44) * mm, v(74.94, -400.1) * mm, v(29.16, -466.89) * mm, v(19.52, -535.33) * mm, v(47.3, -548.4) * mm, v(56.5, -545.64) * mm]});
            skFitSpline(sketch, "E54.1.17", {"points": [v(56.5, -545.64) * mm, v(66.4, -542.67) * mm, v(81.9, -516.59) * mm, v(74.38, -475.12) * mm, v(109.7, -394.88) * mm, v(209.15, -376.97) * mm, v(204.78, -363.34) * mm, v(203.26, -361.4) * mm]});
            skFitSpline(sketch, "E54.1.18", {"points": [v(146.46, -370.89) * mm, v(149.37, -384.28) * mm, v(217.45, -370.96) * mm, v(251.93, -257.59) * mm, v(235.9, 87.94) * mm, v(246.84, 187.31) * mm, v(279.66, 211.8) * mm, v(276.66, 188.43) * mm, v(291.6, 220.03) * mm]});
            skFitSpline(sketch, "E54.1.19", {"points": [v(291.6, 220.03) * mm, v(299.11, 235.11) * mm, v(190.89, 240.63) * mm, v(259.32, 16.49) * mm, v(120.9, -227.85) * mm, v(146.46, -370.89) * mm]});
            skLineSegment(sketch, "E54.1.20", {"start": v(241.11, 224.77) * mm, "end": v(248.05, 217.78) * mm});
            skLineSegment(sketch, "E54.1.21", {"start": v(248.05, 217.78) * mm, "end": v(244.38, 214.16) * mm});
            skFitSpline(sketch, "E55.0", {"points": [v(-291.6, 220.03) * mm, v(-299.11, 235.11) * mm, v(-190.89, 240.63) * mm, v(-259.32, 16.49) * mm, v(-120.9, -227.85) * mm, v(-146.46, -370.89) * mm]});
            skFitSpline(sketch, "E56.0", {"points": [v(-291.6, 220.03) * mm, v(-276.66, 188.43) * mm, v(-279.66, 211.8) * mm, v(-246.84, 187.31) * mm, v(-235.9, 87.94) * mm, v(-251.93, -257.59) * mm, v(-217.45, -370.96) * mm, v(-149.37, -384.28) * mm, v(-146.46, -370.89) * mm]});
            skFitSpline(sketch, "E57.0", {"points": [v(-291.6, 220.03) * mm, v(-299.11, 235.11) * mm, v(-190.89, 240.63) * mm, v(-259.32, 16.49) * mm, v(-120.9, -227.85) * mm, v(-146.46, -370.89) * mm]});
            skFitSpline(sketch, "E58.0", {"points": [v(-291.6, 220.03) * mm, v(-299.11, 235.11) * mm, v(-190.89, 240.63) * mm, v(-259.32, 16.49) * mm, v(-120.9, -227.85) * mm, v(-146.46, -370.89) * mm]});
            skLineSegment(sketch, "E59.0", {"start": v(-244.38, 214.16) * mm, "end": v(-248.05, 217.78) * mm});
            skLineSegment(sketch, "E60.0", {"start": v(-248.05, 217.78) * mm, "end": v(-241.11, 224.77) * mm});
            skLineSegment(sketch, "E61.0", {"start": v(-223.83, 203.2) * mm, "end": v(-231.23, 203.2) * mm});
            skLineSegment(sketch, "E62.0", {"start": v(-222.22, 198.44) * mm, "end": v(-231.23, 198.44) * mm});
            skLineSegment(sketch, "E63.0", {"start": v(-231.23, 198.44) * mm, "end": v(-231.23, 203.2) * mm});
            skLineSegment(sketch, "E64.0", {"start": v(-244.38, 214.16) * mm, "end": v(-236.83, 221.78) * mm});
            skLineSegment(sketch, "E65.0", {"start": v(-144.14, -355.6) * mm, "end": v(-149.22, -355.6) * mm});
            skLineSegment(sketch, "E66.0", {"start": v(-143.58, -350.84) * mm, "end": v(-149.22, -350.84) * mm});
            skLineSegment(sketch, "E67.0", {"start": v(-149.22, -350.84) * mm, "end": v(-149.22, -355.6) * mm});
            skPoint(sketch, "E68.orphan", {"position": v(-244.59, 214.37) * mm});
            skPoint(sketch, "E69.orphan", {"position": v(-260.03, 198.38) * mm});
            skLineSegment(sketch, "E70", {"start": v(-223.83, 203.2) * mm, "end": v(-204.78, 203.2) * mm});
            skLineSegment(sketch, "E71", {"start": v(-236.83, 221.78) * mm, "end": v(-219.71, 239.04) * mm});
            skArc(sketch, "E72", {"start": v(-204.78, 203.2) * mm, "mid": v(-208.66, 222.61) * mm, "end": v(-219.71, 239.04) * mm});
            skArc(sketch, "E73", {"start": v(219.71, 239.04) * mm, "mid": v(208.66, 222.61) * mm, "end": v(204.78, 203.2) * mm});
            skLineSegment(sketch, "E74", {"start": v(223.83, 203.2) * mm, "end": v(231.23, 203.2) * mm});
            skPoint(sketch, "E75.orphan", {"position": v(244.59, 214.37) * mm});
            skLineSegment(sketch, "E76.trimOffspring", {"start": v(244.38, 214.16) * mm, "end": v(219.71, 239.04) * mm});
            skSolve(sketch);
        }
        {
            var Q0;
            Q0 = qSketchRegion(id + "F21", true);
            extrude(context, id + "F22", {"entities" : qUnion([Q0]), "depth" : 258.76 * mm, "hasSecondDirection" : true, "secondDirectionOppositeDirection" : false, "secondDirectionDepth" : 254 * mm});
        }
    });
